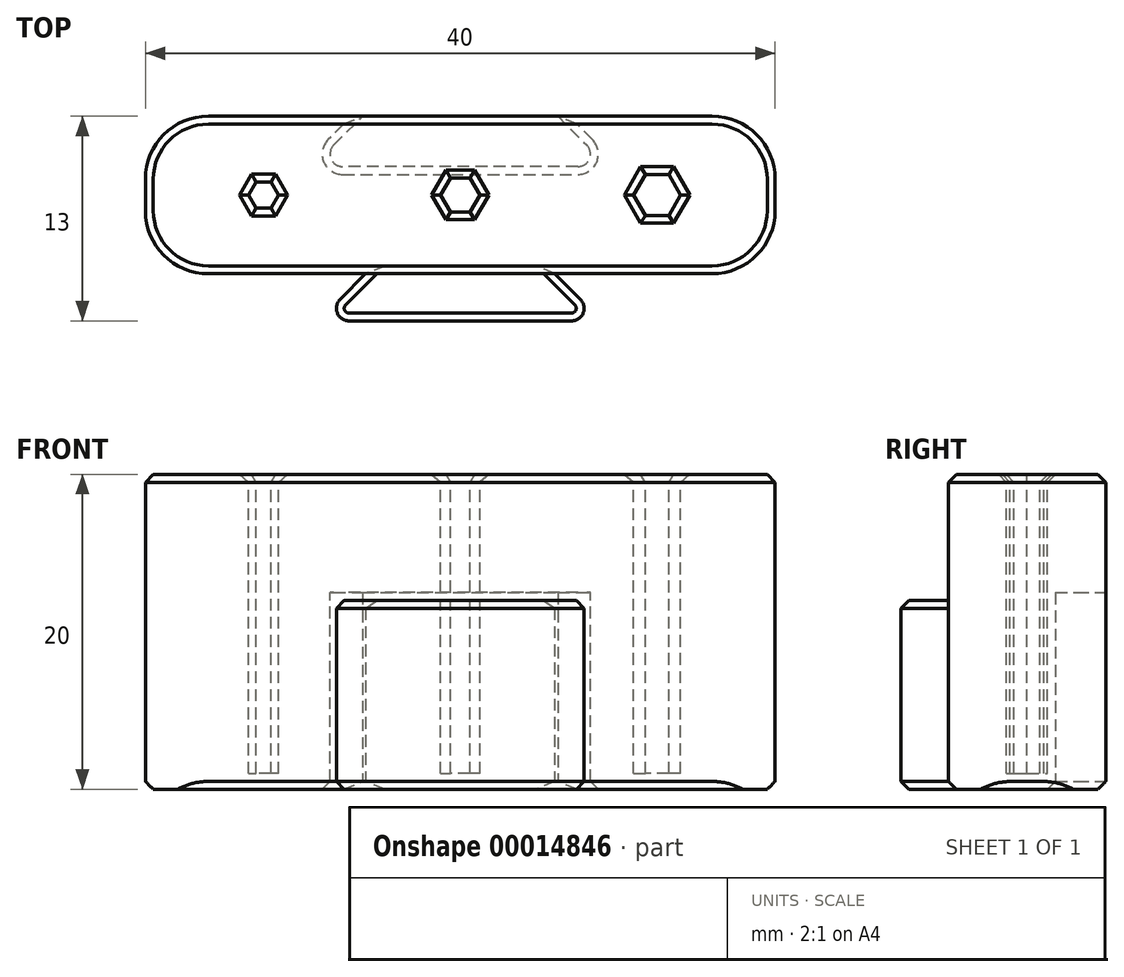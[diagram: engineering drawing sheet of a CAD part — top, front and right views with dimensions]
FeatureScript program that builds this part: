
annotation { "Feature Type Name" : "Feature", "Feature Type Description" : "" }
export const myFeature = defineFeature(function(context is Context, id is Id, definition is map)
    precondition{}
    {
        {
            var Q0;
            Q0=qCreatedBy(makeId("Top.planeOp"),FACE);
            var sketch = newSketch(context, id + "F0", { "sketchPlane" : qUnion([Q0])});
            skLineSegment(sketch, "E0.bottom", {"start": v(0, 0) * mm, "end": v(40, 0) * mm});
            skLineSegment(sketch, "E0.top", {"start": v(0, 10) * mm, "end": v(40, 10) * mm});
            skLineSegment(sketch, "E0.left", {"start": v(0, 0) * mm, "end": v(0, 10) * mm});
            skLineSegment(sketch, "E0.right", {"start": v(40, 0) * mm, "end": v(40, 10) * mm});
            skLineSegment(sketch, "E1", {"start": v(0, 5) * mm, "end": v(40, 5) * mm, "construction": true});
            skLineSegment(sketch, "E2", {"start": v(20, 10) * mm, "end": v(20, 0) * mm, "construction": true});
            skLineSegment(sketch, "E3", {"start": v(14, 0) * mm, "end": v(11, -3) * mm});
            skLineSegment(sketch, "E4", {"start": v(11, -3) * mm, "end": v(29, -3) * mm});
            skLineSegment(sketch, "E5", {"start": v(29, -3) * mm, "end": v(26, 0) * mm});
            skLineSegment(sketch, "E6", {"start": v(26.2, 10) * mm, "end": v(29.4, 6.8) * mm});
            skLineSegment(sketch, "E7", {"start": v(29.4, 6.8) * mm, "end": v(10.6, 6.8) * mm});
            skLineSegment(sketch, "E8", {"start": v(10.6, 6.8) * mm, "end": v(13.8, 10) * mm});
            skSolve(sketch);
        }
        {
            var Q0;
            {var subQ1=sQuery(id+"F0.wireOp",EDGE,"E6");Q0=makeQuery(id+"F0.imprint","IMPRINT",FACE,{"disambiguationData":[TD([[makeQuery(id+"F0.imprint","IMPRINT",EDGE,{"derivedFrom":subQ1}),-1.0]])]});}
            var Q1;
            {var subQ1=sQuery(id+"F0.wireOp",EDGE,"ca3dedec-cce3-4ce7-b49e-b633109c9dc3");Q1=makeQuery(id+"F0.imprint","IMPRINT",FACE,{"disambiguationData":[TD([[makeQuery(id+"F0.imprint","IMPRINT",EDGE,{"derivedFrom":subQ1}),-1.0]])]});}
            var Q2;
            {var subQ2=sQuery(id+"F0.wireOp",EDGE,"E0.left");Q2=makeQuery(id+"F0.imprint","IMPRINT",FACE,{"disambiguationData":[TD([[makeQuery(id+"F0.imprint","IMPRINT",EDGE,{"derivedFrom":subQ2}),-1.0]])]});}
            extrude(context, id + "F1", {"entities" : qUnion([Q0, Q1, Q2]), "depth" : 20 * mm});
        }
        {
            var Q0;
            {var subQ1=sQuery(id+"F0.wireOp",EDGE,"E3");Q0=makeQuery(id+"F0.imprint","IMPRINT",FACE,{"disambiguationData":[TD([[makeQuery(id+"F0.imprint","IMPRINT",EDGE,{"derivedFrom":subQ1}),1.0]])]});}
            var Q1;
            {var subQ1=sQuery(id+"F0.wireOp",EDGE,"6b10c7fe-a54a-4345-beb3-36d7e7544fd5");Q1=makeQuery(id+"F0.imprint","IMPRINT",FACE,{"disambiguationData":[TD([[makeQuery(id+"F0.imprint","IMPRINT",EDGE,{"derivedFrom":subQ1}),-1.0]])]});}
            extrude(context, id + "F2", {"entities" : qUnion([Q0, Q1]), "operationType" : NewBodyOperationType.ADD, "depth" : 12 * mm});
        }
        {
            var Q0;
            {var subQ1=sQuery(id+"F0.wireOp",EDGE,"E6");Q0=makeQuery(id+"F0.imprint","IMPRINT",FACE,{"disambiguationData":[TD([[makeQuery(id+"F0.imprint","IMPRINT",EDGE,{"derivedFrom":subQ1}),-1.0]])]});}
            var Q1;
            {var subQ1=sQuery(id+"F0.wireOp",EDGE,"ca3dedec-cce3-4ce7-b49e-b633109c9dc3");Q1=makeQuery(id+"F0.imprint","IMPRINT",FACE,{"disambiguationData":[TD([[makeQuery(id+"F0.imprint","IMPRINT",EDGE,{"derivedFrom":subQ1}),-1.0]])]});}
            extrude(context, id + "F3", {"entities" : qUnion([Q0, Q1]), "operationType" : NewBodyOperationType.REMOVE, "depth" : 12.5 * mm});
        }
        {
            var Q0;
            Q0=makeQuery(id+"F3.boolean.opBoolean","COPY",EDGE,{"derivedFrom":makeQuery(id+"F3.opExtrude","SWEPT_EDGE",EDGE,{"disambiguationData":[OSD([sQuery(id+"F0.wireOp",EDGE,"E0.right"),sQuery(id+"F0.wireOp",EDGE,"dda16c34-c5be-4889-a8f6-527097e57128")])]})});
            var Q1;
            Q1=makeQuery(id+"F3.boolean.opBoolean","COPY",EDGE,{"derivedFrom":makeQuery(id+"F3.opExtrude","SWEPT_EDGE",EDGE,{"disambiguationData":[OSD([sQuery(id+"F0.wireOp",EDGE,"3c9dca09-d959-4067-9121-8a6dfe8b8fca"),sQuery(id+"F0.wireOp",EDGE,"dda16c34-c5be-4889-a8f6-527097e57128")])]})});
            var Q2;
            Q2=makeQuery(id+"F3.boolean.opBoolean","COPY",EDGE,{"derivedFrom":makeQuery(id+"F3.opExtrude","SWEPT_EDGE",EDGE,{"disambiguationData":[OSD([sQuery(id+"F0.wireOp",EDGE,"E0.right"),sQuery(id+"F0.wireOp",EDGE,"ca3dedec-cce3-4ce7-b49e-b633109c9dc3")])]})});
            var Q3;
            Q3=makeQuery(id+"F2.opExtrude","SWEPT_EDGE",EDGE,{"disambiguationData":[OSD([sQuery(id+"F0.wireOp",EDGE,"E4"),sQuery(id+"F0.wireOp",EDGE,"E5")])]});
            var Q4;
            Q4=makeQuery(id+"F3.boolean.opBoolean","COPY",EDGE,{"derivedFrom":makeQuery(id+"F3.opExtrude","SWEPT_EDGE",EDGE,{"disambiguationData":[OSD([sQuery(id+"F0.wireOp",EDGE,"ca3dedec-cce3-4ce7-b49e-b633109c9dc3"),sQuery(id+"F0.wireOp",EDGE,"3c9dca09-d959-4067-9121-8a6dfe8b8fca")])]})});
            var Q5;
            Q5=makeQuery(id+"F3.boolean.opBoolean","COPY",EDGE,{"derivedFrom":makeQuery(id+"F3.opExtrude","SWEPT_EDGE",EDGE,{"disambiguationData":[OSD([sQuery(id+"F0.wireOp",EDGE,"E0.top"),sQuery(id+"F0.wireOp",EDGE,"E8")])]})});
            var Q6;
            Q6=makeQuery(id+"F3.boolean.opBoolean","COPY",EDGE,{"derivedFrom":makeQuery(id+"F3.opExtrude","SWEPT_EDGE",EDGE,{"disambiguationData":[OSD([sQuery(id+"F0.wireOp",EDGE,"E0.top"),sQuery(id+"F0.wireOp",EDGE,"E6")])]})});
            var Q7;
            Q7=makeQuery(id+"F3.boolean.opBoolean","COPY",EDGE,{"derivedFrom":makeQuery(id+"F3.opExtrude","SWEPT_EDGE",EDGE,{"disambiguationData":[OSD([sQuery(id+"F0.wireOp",EDGE,"E7"),sQuery(id+"F0.wireOp",EDGE,"E8")])]})});
            var Q8;
            Q8=makeQuery(id+"F3.boolean.opBoolean","COPY",EDGE,{"derivedFrom":makeQuery(id+"F3.opExtrude","SWEPT_EDGE",EDGE,{"disambiguationData":[OSD([sQuery(id+"F0.wireOp",EDGE,"E6"),sQuery(id+"F0.wireOp",EDGE,"E7")])]})});
            var Q9;
            Q9=makeQuery(id+"F2.opExtrude","SWEPT_EDGE",EDGE,{"disambiguationData":[OSD([sQuery(id+"F0.wireOp",EDGE,"2ee69dbe-8a32-4f72-af18-887ad2213329"),sQuery(id+"F0.wireOp",EDGE,"aeb38691-0133-48aa-a3ed-6e955bb906ba")])]});
            var Q10;
            Q10=makeQuery(id+"F2.opExtrude","SWEPT_EDGE",EDGE,{"disambiguationData":[OSD([sQuery(id+"F0.wireOp",EDGE,"E0.left"),sQuery(id+"F0.wireOp",EDGE,"aeb38691-0133-48aa-a3ed-6e955bb906ba")])]});
            var Q11;
            Q11=makeQuery(id+"F2.opExtrude","SWEPT_EDGE",EDGE,{"disambiguationData":[OSD([sQuery(id+"F0.wireOp",EDGE,"E0.left"),sQuery(id+"F0.wireOp",EDGE,"6b10c7fe-a54a-4345-beb3-36d7e7544fd5")])]});
            var Q12;
            Q12=makeQuery(id+"F2.opExtrude","SWEPT_EDGE",EDGE,{"disambiguationData":[OSD([sQuery(id+"F0.wireOp",EDGE,"6b10c7fe-a54a-4345-beb3-36d7e7544fd5"),sQuery(id+"F0.wireOp",EDGE,"2ee69dbe-8a32-4f72-af18-887ad2213329")])]});
            var Q13;
            Q13=makeQuery(id+"F2.opExtrude","SWEPT_EDGE",EDGE,{"disambiguationData":[OSD([sQuery(id+"F0.wireOp",EDGE,"E3"),sQuery(id+"F0.wireOp",EDGE,"E4")])]});
            var Q14;
            Q14=makeQuery(id+"F2.opExtrude","SWEPT_EDGE",EDGE,{"disambiguationData":[OSD([sQuery(id+"F0.wireOp",EDGE,"E0.bottom"),sQuery(id+"F0.wireOp",EDGE,"E3")])]});
            var Q15;
            Q15=makeQuery(id+"F2.opExtrude","SWEPT_EDGE",EDGE,{"disambiguationData":[OSD([sQuery(id+"F0.wireOp",EDGE,"E0.bottom"),sQuery(id+"F0.wireOp",EDGE,"E5")])]});
            fillet(context, id + "F4", {"entities" : qUnion([Q0, Q1, Q2, Q3, Q4, Q5, Q6, Q7, Q8, Q9, Q10, Q11, Q12, Q13, Q14, Q15]), "radius" : .8 * mm, "tangentPropagation" : true, "allowEdgeOverflow" : false});
        }
        {
            var Q0;
            Q0=makeQuery(id+"F2.opExtrude","CAP_EDGE",EDGE,{"disambiguationData":[OSD([sQuery(id+"F0.wireOp",EDGE,"E4")])],"isStart":false});
            var Q1;
            Q1=makeQuery(id+"F2.opExtrude","CAP_EDGE",EDGE,{"disambiguationData":[OSD([sQuery(id+"F0.wireOp",EDGE,"2ee69dbe-8a32-4f72-af18-887ad2213329")])],"isStart":false});
            chamfer(context, id + "F5", {"entities" : qUnion([Q0, Q1]), "width" : .5 * mm, "tangentPropagation" : true});
        }
        {
            var Q0;
            {var subQ0=sQuery(id+"F0.wireOp",EDGE,"E0.bottom");Q0=makeQuery(id+"F2.boolean.opBoolean","MERGE",FACE,{"derivedFrom":[makeQuery(id+"F1.opExtrude","CAP_FACE",FACE,{"disambiguationData":[OSD([subQ0,sQuery(id+"F0.wireOp",EDGE,"E0.top"),sQuery(id+"F0.wireOp",EDGE,"E0.left"),sQuery(id+"F0.wireOp",EDGE,"E0.right")])],"isStart":true}),makeQuery(id+"F2.opExtrude","CAP_FACE",FACE,{"disambiguationData":[OSD([subQ0,sQuery(id+"F0.wireOp",EDGE,"E3"),sQuery(id+"F0.wireOp",EDGE,"E4"),sQuery(id+"F0.wireOp",EDGE,"E5")])],"isStart":true})]});}
            chamfer(context, id + "F6", {"entities" : qUnion([Q0]), "width" : .5 * mm, "tangentPropagation" : true});
        }
        {
            var Q0;
            Q0=makeQuery(id+"F1.opExtrude","CAP_FACE",FACE,{"disambiguationData":[OSD([sQuery(id+"F0.wireOp",EDGE,"E0.bottom"),sQuery(id+"F0.wireOp",EDGE,"E0.top"),sQuery(id+"F0.wireOp",EDGE,"E0.left"),sQuery(id+"F0.wireOp",EDGE,"E0.right")])],"isStart":false});
            var sketch = newSketch(context, id + "F7", { "sketchPlane" : qUnion([Q0])});
            skCircle(sketch, "E9.cCircle", {"center": v(32.5, 5) * mm, "radius": 1.5 * mm, "construction": true});
            skLineSegment(sketch, "E9.0", {"start": v(31, 5) * mm, "end": v(31.75, 6.3) * mm});
            skLineSegment(sketch, "E9.1", {"start": v(31.75, 6.3) * mm, "end": v(33.25, 6.3) * mm});
            skLineSegment(sketch, "E9.2", {"start": v(33.25, 6.3) * mm, "end": v(34, 5) * mm});
            skLineSegment(sketch, "E9.3", {"start": v(34, 5) * mm, "end": v(33.25, 3.7) * mm});
            skLineSegment(sketch, "E9.4", {"start": v(33.25, 3.7) * mm, "end": v(31.75, 3.7) * mm});
            skLineSegment(sketch, "E9.5", {"start": v(31.75, 3.7) * mm, "end": v(31, 5) * mm});
            skCircle(sketch, "E10.cCircle", {"center": v(20, 5) * mm, "radius": 1.24 * mm, "construction": true});
            skLineSegment(sketch, "E10.0", {"start": v(18.76, 5) * mm, "end": v(19.38, 6.07) * mm});
            skLineSegment(sketch, "E10.1", {"start": v(19.38, 6.07) * mm, "end": v(20.62, 6.07) * mm});
            skLineSegment(sketch, "E10.2", {"start": v(20.62, 6.08) * mm, "end": v(21.24, 5) * mm});
            skLineSegment(sketch, "E10.3", {"start": v(21.24, 5) * mm, "end": v(20.62, 3.92) * mm});
            skLineSegment(sketch, "E10.4", {"start": v(20.62, 3.92) * mm, "end": v(19.38, 3.92) * mm});
            skLineSegment(sketch, "E10.5", {"start": v(19.38, 3.93) * mm, "end": v(18.76, 5) * mm});
            skCircle(sketch, "E11.cCircle", {"center": v(7.5, 5) * mm, "radius": 0.95 * mm, "construction": true});
            skLineSegment(sketch, "E11.0", {"start": v(6.55, 5) * mm, "end": v(7.02, 5.83) * mm});
            skLineSegment(sketch, "E11.1", {"start": v(7.02, 5.82) * mm, "end": v(7.98, 5.82) * mm});
            skLineSegment(sketch, "E11.2", {"start": v(7.98, 5.83) * mm, "end": v(8.45, 5) * mm});
            skLineSegment(sketch, "E11.3", {"start": v(8.45, 5) * mm, "end": v(7.98, 4.18) * mm});
            skLineSegment(sketch, "E11.4", {"start": v(7.98, 4.18) * mm, "end": v(7.02, 4.17) * mm});
            skLineSegment(sketch, "E11.5", {"start": v(7.02, 4.17) * mm, "end": v(6.55, 5) * mm});
            skLineSegment(sketch, "E12", {"start": v(20, 10) * mm, "end": v(20, 0) * mm, "construction": true});
            skLineSegment(sketch, "E13", {"start": v(0, 5) * mm, "end": v(40, 5) * mm, "construction": true});
            skSolve(sketch);
        }
        {
            var Q0;
            Q0=makeQuery(id+"F7.imprint","IMPRINT",FACE,{"disambiguationData":[TD([[makeQuery(id+"F7.imprint","IMPRINT",EDGE,{"derivedFrom":sQuery(id+"F7.wireOp",EDGE,"E9.0")}),-1.0]])]});
            var Q1;
            Q1=makeQuery(id+"F7.imprint","IMPRINT",FACE,{"disambiguationData":[TD([[makeQuery(id+"F7.imprint","IMPRINT",EDGE,{"derivedFrom":sQuery(id+"F7.wireOp",EDGE,"E10.0")}),-1.0]])]});
            var Q2;
            Q2=makeQuery(id+"F7.imprint","IMPRINT",FACE,{"disambiguationData":[TD([[makeQuery(id+"F7.imprint","IMPRINT",EDGE,{"derivedFrom":sQuery(id+"F7.wireOp",EDGE,"E11.0")}),-1.0]])]});
            extrude(context, id + "F8", {"entities" : qUnion([Q0, Q1, Q2]), "operationType" : NewBodyOperationType.REMOVE, "oppositeDirection" : true, "depth" : 19 * mm});
        }
        {
            var Q0;
            Q0=makeQuery(id+"F1.opExtrude","SWEPT_EDGE",EDGE,{"disambiguationData":[OSD([sQuery(id+"F0.wireOp",EDGE,"E0.bottom"),sQuery(id+"F0.wireOp",EDGE,"E0.left")])]});
            var Q1;
            Q1=makeQuery(id+"F1.opExtrude","SWEPT_EDGE",EDGE,{"disambiguationData":[OSD([sQuery(id+"F0.wireOp",EDGE,"E0.bottom"),sQuery(id+"F0.wireOp",EDGE,"E0.right")])]});
            var Q2;
            Q2=makeQuery(id+"F1.opExtrude","SWEPT_EDGE",EDGE,{"disambiguationData":[OSD([sQuery(id+"F0.wireOp",EDGE,"E0.top"),sQuery(id+"F0.wireOp",EDGE,"E0.right")])]});
            var Q3;
            Q3=makeQuery(id+"F1.opExtrude","SWEPT_EDGE",EDGE,{"disambiguationData":[OSD([sQuery(id+"F0.wireOp",EDGE,"E0.top"),sQuery(id+"F0.wireOp",EDGE,"E0.left")])]});
            fillet(context, id + "F9", {"entities" : qUnion([Q0, Q1, Q2, Q3]), "radius" : 4 * mm, "tangentPropagation" : true, "allowEdgeOverflow" : false});
        }
        {
            var Q0;
            Q0=makeQuery(id+"F1.opExtrude","CAP_FACE",FACE,{"disambiguationData":[OSD([sQuery(id+"F0.wireOp",EDGE,"E0.bottom"),sQuery(id+"F0.wireOp",EDGE,"E0.top"),sQuery(id+"F0.wireOp",EDGE,"E0.left"),sQuery(id+"F0.wireOp",EDGE,"E0.right")])],"isStart":false});
            chamfer(context, id + "F10", {"entities" : qUnion([Q0]), "width" : .5 * mm, "tangentPropagation" : true});
        }
    });
